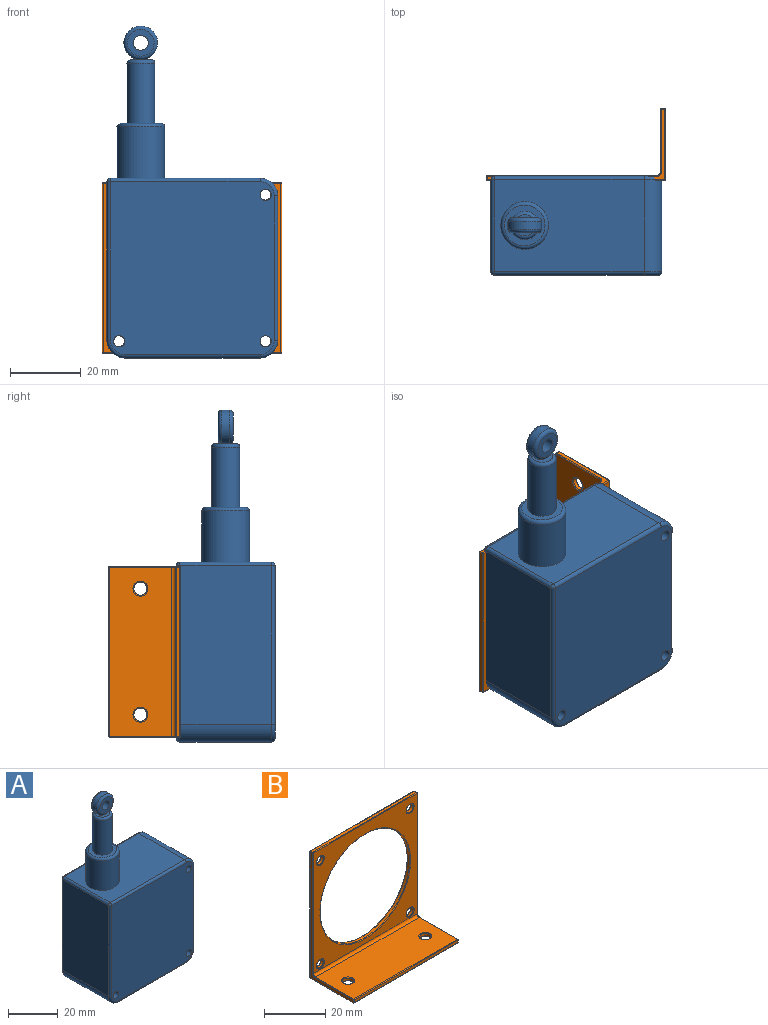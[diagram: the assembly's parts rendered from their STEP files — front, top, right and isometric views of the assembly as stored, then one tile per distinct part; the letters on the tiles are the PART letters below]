
ASSEMBLY  parts=2 mates=1
PART A: 41 faces, bbox 49.1x27.9x94.6 mm
  f0: plane 40.8x25.9mm, normal (1,0,0), area 1056.7mm2, adj f14,f15,f18,f27
  f1: plane 42.3x25.9mm, normal (0,0,1), area 952.4mm2, adj f9,f14,f16,f22,f31
  f2: plane 44.8x25.9mm, normal (-1,0,0), area 1160.3mm2, adj f13,f16,f23,f30
  f3: cylinder r=1.59mm len=27.9mm, axis (0,1,0), area 278.3mm2, adj f7,f8
  f4: cylinder r=1.59mm len=27.9mm, axis (0,1,0), area 278.3mm2, adj f7,f8
  f5: plane 38.3x25.9mm, normal (0,0,-1), area 992mm2, adj f13,f15,f19,f26
  f6: cylinder r=1.59mm len=27.9mm, axis (0,1,0), area 278.3mm2, adj f7,f8
  f7: plane 48.8x46.3mm, normal (0,-1,0), area 2225.4mm2, adj f3,f4,f6,f17,f18,f19,f20,f21
  f8: plane 48.8x46.3mm, normal (0,1,0), area 2225.4mm2, adj f3,f4,f6,f25,f26,f27,f28,f29
  f9: cylinder r=6.75mm len=14.5mm, axis (0,0,-1), area 615mm2, adj f1,f33
  f10: plane 11.5x11.5mm, normal (0,0,1), area 53.6mm2, adj f11,f33
  f11: cylinder r=4mm len=17mm, axis (0,0,-1), area 427.3mm2, adj f10,f40
  f12: plane 6.01x6.01mm, normal (0,0,1), area 28.2mm2, adj f35,f38,f39,f40
  f13: cylinder r=5mm len=25.9mm, axis (0,-1,0), area 203.4mm2, adj f2,f5,f21,f28
  f14: cylinder r=5mm len=25.9mm, axis (0,-1,0), area 203.4mm2, adj f0,f1,f20,f29
  f15: cylinder r=5mm len=25.9mm, axis (0,1,0), area 203.4mm2, adj f0,f5,f17,f25
  f16: cylinder r=1mm len=25.9mm, axis (0,1,0), area 40.7mm2, adj f1,f2,f24,f32
  f17: torus R=4mm, axis (0,-1,0), area 11.4mm2, adj f7,f15,f18,f19
  f18: cylinder r=1mm len=40.8mm, axis (0,0,-1), area 64.1mm2, adj f0,f7,f17,f20
  f19: cylinder r=1mm len=38.3mm, axis (-1,0,0), area 60.2mm2, adj f5,f7,f17,f21
  f20: torus R=4mm, axis (0,-1,0), area 11.4mm2, adj f7,f14,f18,f22
  f21: torus R=4mm, axis (0,-1,0), area 11.4mm2, adj f7,f13,f19,f23
  f22: cylinder r=1mm len=42.3mm, axis (1,0,0), area 66.4mm2, adj f1,f7,f20,f24
  f23: cylinder r=1mm len=44.8mm, axis (0,0,1), area 70.4mm2, adj f2,f7,f21,f24
  f24: sphere r=1mm, area 1.6mm2, adj f16,f22,f23
  f25: torus R=4mm, axis (0,-1,0), area 11.4mm2, adj f8,f15,f26,f27
  f26: cylinder r=1mm len=38.3mm, axis (1,0,0), area 60.2mm2, adj f5,f8,f25,f28
  f27: cylinder r=1mm len=40.8mm, axis (0,0,1), area 64.1mm2, adj f0,f8,f25,f29
  f28: torus R=4mm, axis (0,-1,0), area 11.4mm2, adj f8,f13,f26,f30
  f29: torus R=4mm, axis (0,-1,0), area 11.4mm2, adj f8,f14,f27,f31
  f30: cylinder r=1mm len=44.8mm, axis (0,0,-1), area 70.4mm2, adj f2,f8,f28,f32
  f31: cylinder r=1mm len=42.3mm, axis (-1,0,0), area 66.4mm2, adj f1,f8,f29,f32
  f32: sphere r=1mm, area 1.6mm2, adj f16,f30,f31
  f33: torus R=5.75mm, axis (0,0,1), area 63mm2, adj f9,f10
  f34: cylinder r=2.1mm len=4.19mm, axis (0,-1,0), area 55.2mm2, adj f36,f37
  f35: cylinder r=4.76mm len=9.52mm, axis (0,-1,0), area 65.4mm2, adj f12,f38,f39
  f36: plane 7.52x7.52mm, normal (0,1,0), area 30.6mm2, adj f34,f39
  f37: plane 7.52x7.52mm, normal (0,-1,0), area 30.6mm2, adj f34,f38
  f38: torus R=3.76mm, axis (0,1,0), area 43.4mm2, adj f12,f35,f37
  f39: torus R=3.76mm, axis (0,1,0), area 43.4mm2, adj f12,f35,f36
  f40: torus R=3mm, axis (0,0,1), area 35.9mm2, adj f11,f12
PART B: 59 faces, bbox 48.3x20.3x50.8 mm
  f0: plane 47.8x19.8mm, normal (0,0,-1), area 918.7mm2, adj f18,f20,f32,f33,f42,f43
  f1: plane 50.3x47.8mm, normal (0,1,0), area 982.9mm2, adj f16,f22,f24,f26,f28,f31,f32,f40
  f2: plane 47.8x1mm, normal (0,0,1), area 47.8mm2, adj f39,f40,f50,f51
  f3: plane 48.05x47.8mm, normal (0,-1,0), area 875.4mm2, adj f8,f17,f23,f25,f27,f29,f38,f50
  f4: plane 47.8x17.55mm, normal (0,0,1), area 811.2mm2, adj f8,f19,f21,f45,f53,f57
  f5: plane 47.8x1mm, normal (0,-1,0), area 47.8mm2, adj f43,f44,f52,f53
  f6: plane 50.3x19.8mm, normal (1,0,0), area 69.4mm2, adj f41,f42,f51,f52,f56,f57,f58
  f7: plane 50.3x19.8mm, normal (-1,0,0), area 69.4mm2, adj f31,f33,f37,f38,f39,f44,f45
  f8: cylinder r=1mm len=47.8mm, axis (1,0,0), area 75.1mm2, adj f3,f4,f37,f58
  f9: cylinder r=1.59mm len=3.18mm, axis (0,-1,0), area 10mm2, adj f28,f29
  f10: cylinder r=1.59mm len=3.18mm, axis (0,-1,0), area 10mm2, adj f26,f27
  f11: cylinder r=1.59mm len=3.18mm, axis (0,-1,0), area 10mm2, adj f24,f25
  f12: cylinder r=1.59mm len=3.18mm, axis (0,-1,0), area 10mm2, adj f22,f23
  f13: cylinder r=1.85mm len=3.7mm, axis (0,0,1), area 11.6mm2, adj f20,f21
  f14: cylinder r=1.85mm len=3.7mm, axis (0,0,1), area 11.6mm2, adj f18,f19
  f15: cylinder r=20.7mm len=41.4mm, axis (0,-1,0), area 130.1mm2, adj f16,f17
  f16: torus R=20.95mm, axis (0,1,0), area 51.3mm2, adj f1,f15
  f17: torus R=20.95mm, axis (0,1,0), area 51.3mm2, adj f3,f15
  f18: torus R=2.1mm, axis (0,0,-1), area 4.8mm2, adj f0,f14
  f19: torus R=2.1mm, axis (0,0,-1), area 4.8mm2, adj f4,f14
  f20: torus R=2.1mm, axis (0,0,-1), area 4.8mm2, adj f0,f13
  f21: torus R=2.1mm, axis (0,0,-1), area 4.8mm2, adj f4,f13
  f22: torus R=1.84mm, axis (0,1,0), area 4.1mm2, adj f1,f12
  f23: torus R=1.84mm, axis (0,1,0), area 4.1mm2, adj f3,f12
  f24: torus R=1.84mm, axis (0,1,0), area 4.1mm2, adj f1,f11
  f25: torus R=1.84mm, axis (0,1,0), area 4.1mm2, adj f3,f11
  f26: torus R=1.84mm, axis (0,1,0), area 4.1mm2, adj f1,f10
  f27: torus R=1.84mm, axis (0,1,0), area 4.1mm2, adj f3,f10
  f28: torus R=1.84mm, axis (0,1,0), area 4.1mm2, adj f1,f9
  f29: torus R=1.84mm, axis (0,1,0), area 4.1mm2, adj f3,f9
  f30: sphere r=0.25mm, area 0.1mm2, adj f31,f32,f33
  f31: cylinder r=0.25mm len=50.3mm, axis (0,0,1), area 19.8mm2, adj f1,f7,f30,f34
  f32: cylinder r=0.25mm len=47.8mm, axis (-1,0,0), area 18.8mm2, adj f0,f1,f30,f35
  f33: cylinder r=0.25mm len=19.8mm, axis (0,1,0), area 7.8mm2, adj f0,f7,f30,f36
  f34: sphere r=0.25mm, area 0.1mm2, adj f31,f39,f40
  f35: sphere r=0.25mm, area 0.1mm2, adj f32,f41,f42
  f36: sphere r=0.25mm, area 0.1mm2, adj f33,f43,f44
  f37: torus R=1.25mm, axis (1,0,0), area 0.7mm2, adj f7,f8,f38,f45
  f38: cylinder r=0.25mm len=48.05mm, axis (0,0,-1), area 18.9mm2, adj f3,f7,f37,f46
  f39: cylinder r=0.25mm len=1mm, axis (0,-1,0), area 0.4mm2, adj f2,f7,f34,f46
  f40: cylinder r=0.25mm len=47.8mm, axis (1,0,0), area 18.8mm2, adj f1,f2,f34,f47
  f41: cylinder r=0.25mm len=50.3mm, axis (0,0,-1), area 19.8mm2, adj f1,f6,f35,f47
  f42: cylinder r=0.25mm len=19.8mm, axis (0,-1,0), area 7.8mm2, adj f0,f6,f35,f48
  f43: cylinder r=0.25mm len=47.8mm, axis (-1,0,0), area 18.8mm2, adj f0,f5,f36,f48
  f44: cylinder r=0.25mm len=1mm, axis (0,0,-1), area 0.4mm2, adj f5,f7,f36,f49
  f45: cylinder r=0.25mm len=17.55mm, axis (0,-1,0), area 6.9mm2, adj f4,f7,f37,f49
  f46: sphere r=0.25mm, area 0.1mm2, adj f38,f39,f50
  f47: sphere r=0.25mm, area 0.1mm2, adj f40,f41,f51
  f48: sphere r=0.25mm, area 0.1mm2, adj f42,f43,f52
  f49: sphere r=0.25mm, area 0.1mm2, adj f44,f45,f53
  f50: cylinder r=0.25mm len=47.8mm, axis (-1,0,0), area 18.8mm2, adj f2,f3,f46,f54
  f51: cylinder r=0.25mm len=1mm, axis (0,1,0), area 0.4mm2, adj f2,f6,f47,f54
  f52: cylinder r=0.25mm len=1mm, axis (0,0,1), area 0.4mm2, adj f5,f6,f48,f55
  f53: cylinder r=0.25mm len=47.8mm, axis (1,0,0), area 18.8mm2, adj f4,f5,f49,f55
  f54: sphere r=0.25mm, area 0.1mm2, adj f50,f51,f56
  f55: sphere r=0.25mm, area 0.1mm2, adj f52,f53,f57
  f56: cylinder r=0.25mm len=48.05mm, axis (0,0,1), area 18.9mm2, adj f3,f6,f54,f58
  f57: cylinder r=0.25mm len=17.55mm, axis (0,1,0), area 6.9mm2, adj f4,f6,f55,f58
  f58: torus R=1.25mm, axis (1,0,0), area 0.7mm2, adj f6,f8,f56,f57
PLACE A at identity
PLACE B rot(axis=(-0.71,0,0.71),180deg) t=(-0.11,-0.5,24.26)mm
MATE fastened B.f15 <-> A.f8  axis (0,-1,0) through (-0.11,0,0.11)mm
